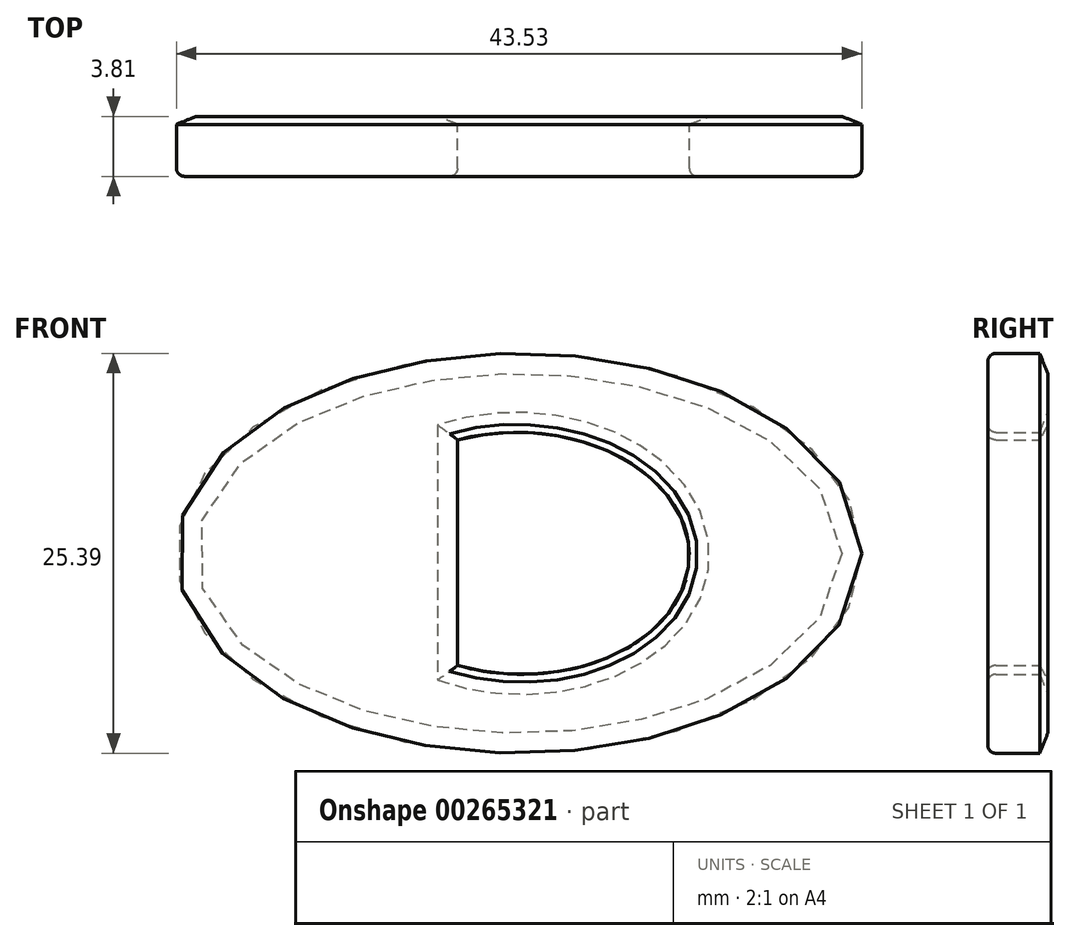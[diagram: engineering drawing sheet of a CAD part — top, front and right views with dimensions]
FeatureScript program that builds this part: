
annotation { "Feature Type Name" : "Feature", "Feature Type Description" : "" }
export const myFeature = defineFeature(function(context is Context, id is Id, definition is map)
    precondition{}
    {
        {
            var Q0;
            Q0=qCreatedBy(makeId("Front.planeOp"),FACE);
            var sketch = newSketch(context, id + "F0", { "sketchPlane" : qUnion([Q0])});
            skPoint(sketch, "E0.middle", {"position": v(7.84, -0.5) * mm});
            skEllipse(sketch, "E1", {"center": v(7.38, -0.18) * mm, "majorRadius": 22.68 * mm, "minorRadius": 13.57 * mm, "majorAxis": v(1, 0)});
            skEllipse(sketch, "E2", {"center": v(7.38, -0.18) * mm, "majorRadius": 21.77 * mm, "minorRadius": 12.7 * mm, "majorAxis": v(1, 0)});
            skEllipticalArc(sketch, "E3", {});
            skLineSegment(sketch, "E4", {"start": v(3.48, 7.03) * mm, "end": v(3.48, -7.3) * mm});
            skLineSegment(sketch, "E5.0", {"start": v(-5.63, 5.88) * mm, "end": v(-5.63, -5.22) * mm});
            skFitSpline(sketch, "E6.0", {"points": [v(27.34, -1.74) * mm, v(27.46, -0.63) * mm, v(27.4, 0.49) * mm, v(27.05, 1.96) * mm, v(26.33, 3.4) * mm, v(25.25, 4.8) * mm, v(23.93, 6.12) * mm, v(21.89, 7.64) * mm, v(19.37, 8.9) * mm, v(17.12, 9.74) * mm, v(14.75, 10.45) * mm, v(12.23, 10.95) * mm, v(9.63, 11.23) * mm, v(7.64, 11.33) * mm, v(5.65, 11.32) * mm, v(3.04, 11.16) * mm, v(0.5, 10.77) * mm, v(-1.9, 10.17) * mm, v(-4.19, 9.43) * mm, v(-6.75, 8.28) * mm, v(-8.87, 6.87) * mm, v(-10.24, 5.6) * mm, v(-11.39, 4.26) * mm, v(-12.17, 2.85) * mm, v(-12.58, 1.39) * mm, v(-12.7, 0.28) * mm, v(-12.63, -0.84) * mm, v(-12.28, -2.31) * mm, v(-11.57, -3.76) * mm, v(-10.49, -5.15) * mm, v(-9.17, -6.48) * mm, v(-7.12, -7.99) * mm, v(-4.6, -9.26) * mm, v(-2.35, -10.1) * mm, v(0.02, -10.8) * mm, v(2.54, -11.3) * mm, v(5.14, -11.58) * mm, v(7.12, -11.69) * mm, v(9.1, -11.67) * mm, v(11.72, -11.5) * mm, v(14.26, -11.12) * mm, v(16.66, -10.52) * mm, v(18.95, -9.79) * mm, v(21.52, -8.64) * mm, v(23.63, -7.22) * mm, v(25, -5.95) * mm, v(26.15, -4.61) * mm, v(26.93, -3.2) * mm, v(27.34, -1.74) * mm, v(27.46, -0.63) * mm, v(27.4, 0.49) * mm]});
            skArc(sketch, "E7.0", {"start": v(-10.4, -5.88) * mm, "mid": v(-6.22, -8.53) * mm, "end": v(-1.61, -10.31) * mm});
            skArc(sketch, "E8.0", {"start": v(-9.17, -3.9) * mm, "mid": v(-7.44, -4.66) * mm, "end": v(-5.63, -5.22) * mm});
            skArc(sketch, "E9.0", {"start": v(-5.63, 5.88) * mm, "mid": v(-7.15, 5.24) * mm, "end": v(-8.6, 4.43) * mm});
            skArc(sketch, "E10", {"start": v(-2.12, 10.09) * mm, "mid": v(-6.2, 8.56) * mm, "end": v(-9.97, 6.35) * mm});
            skArc(sketch, "E11", {"start": v(-9.97, 6.35) * mm, "mid": v(-9.42, 5.3) * mm, "end": v(-8.6, 4.43) * mm});
            skArc(sketch, "E12", {"start": v(-9.17, -3.9) * mm, "mid": v(-9.92, -4.8) * mm, "end": v(-10.4, -5.88) * mm});
            skLineSegment(sketch, "E13", {"start": v(-1.61, -10.31) * mm, "end": v(-1.6, -10.31) * mm});
            const initialGuessF0  = {"E3": [0.00738238598922597, -0.0001767332328675062, 0.999744002607619, -0.0226258535772071, 0.010818622442895507, 0.007682466222593672, 4.358951588136364, 1.9563730971985802]};
            skSetInitialGuess(sketch, initialGuessF0);
            skSolve(sketch);
        }
        {
            var Q0;
            Q0=makeQuery(id+"F0.imprint","IMPRINT",FACE,{"disambiguationData":[TD([[makeQuery(id+"F0.imprint","IMPRINT",EDGE,{"derivedFrom":sQuery(id+"F0.wireOp",EDGE,"E3")}),-1.0]])]});
            extrude(context, id + "F1", {"entities" : qUnion([Q0]), "depth" : 3.8 * mm});
        }
        {
            var Q0;
            Q0=makeQuery(id+"F1.opExtrude","CAP_FACE",FACE,{"disambiguationData":[OSD([sQuery(id+"F0.wireOp",EDGE,"E3"),sQuery(id+"F0.wireOp",EDGE,"E4"),sQuery(id+"F0.wireOp",EDGE,"E5.0"),sQuery(id+"F0.wireOp",EDGE,"E6.0"),sQuery(id+"F0.wireOp",EDGE,"E7.0"),sQuery(id+"F0.wireOp",EDGE,"E8.0"),sQuery(id+"F0.wireOp",EDGE,"E9.0"),sQuery(id+"F0.wireOp",EDGE,"E10"),sQuery(id+"F0.wireOp",EDGE,"E11"),sQuery(id+"F0.wireOp",EDGE,"E12"),sQuery(id+"F0.wireOp",EDGE,"E13")])],"isStart":true});
            chamfer(context, id + "F2", {"entities" : qUnion([Q0]), "chamferType" : ChamferType.TWO_OFFSETS, "width1" : 0.5 * mm, "oppositeDirection" : false, "width2" : 1.27 * mm, "tangentPropagation" : true});
        }
        {
            var Q0;
            Q0=makeQuery(id+"F1.opExtrude","CAP_FACE",FACE,{"disambiguationData":[OSD([sQuery(id+"F0.wireOp",EDGE,"E3"),sQuery(id+"F0.wireOp",EDGE,"E4"),sQuery(id+"F0.wireOp",EDGE,"E5.0"),sQuery(id+"F0.wireOp",EDGE,"E6.0"),sQuery(id+"F0.wireOp",EDGE,"E7.0"),sQuery(id+"F0.wireOp",EDGE,"E8.0"),sQuery(id+"F0.wireOp",EDGE,"E9.0"),sQuery(id+"F0.wireOp",EDGE,"E10"),sQuery(id+"F0.wireOp",EDGE,"E11"),sQuery(id+"F0.wireOp",EDGE,"E12"),sQuery(id+"F0.wireOp",EDGE,"E13")])],"isStart":false});
            fillet(context, id + "F3", {"entities" : qUnion([Q0]), "radius" : 0.5 * mm, "tangentPropagation" : true, "allowEdgeOverflow" : false});
        }
    });
